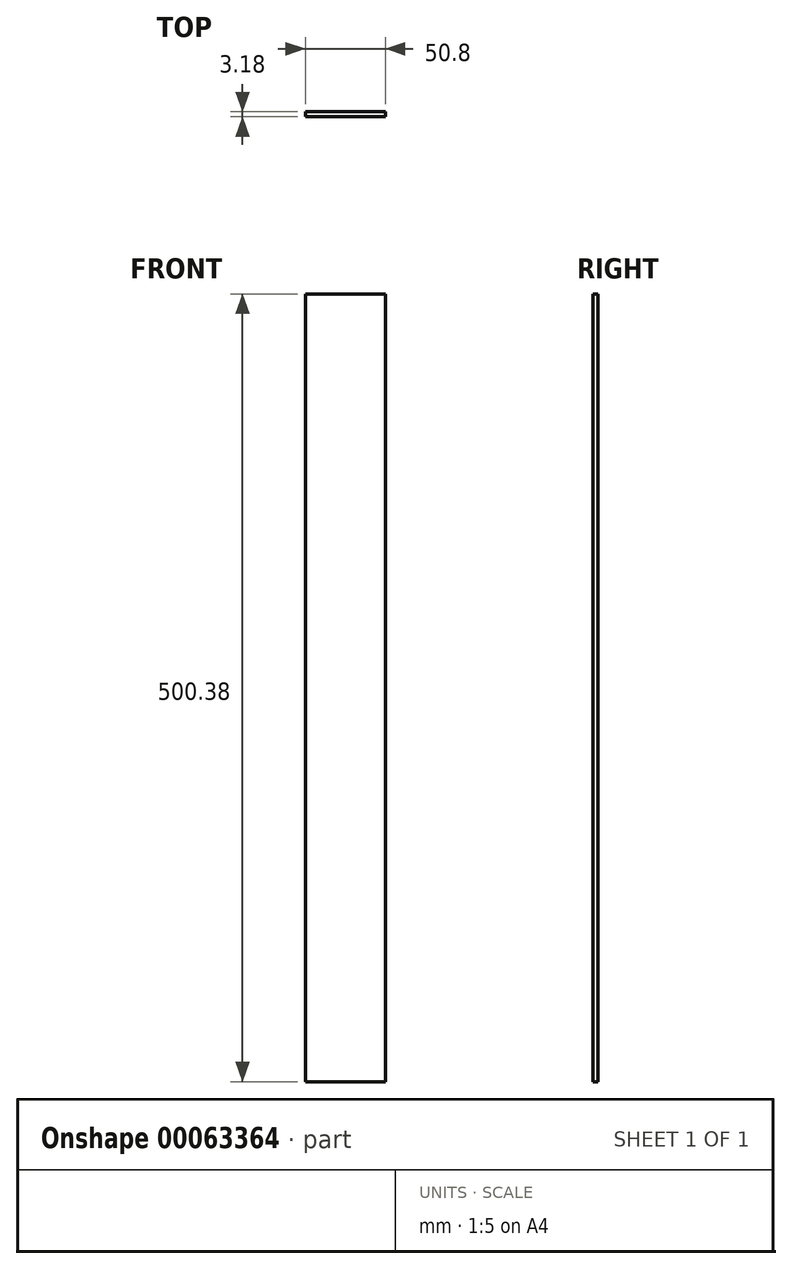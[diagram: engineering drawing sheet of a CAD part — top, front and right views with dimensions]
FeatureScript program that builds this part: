
annotation { "Feature Type Name" : "Feature", "Feature Type Description" : "" }
export const myFeature = defineFeature(function(context is Context, id is Id, definition is map)
    precondition{}
    {
        {
            var Q0;
            Q0=qCreatedBy(makeId("Front.planeOp"),FACE);
            var sketch = newSketch(context, id + "F0", { "sketchPlane" : qUnion([Q0])});
            skLineSegment(sketch, "E0.rect.bottom", {"start": v(25.4, 250.2) * mm, "end": v(-25.4, 250.2) * mm});
            skLineSegment(sketch, "E0.rect.top", {"start": v(25.4, -250.2) * mm, "end": v(-25.4, -250.2) * mm});
            skLineSegment(sketch, "E0.rect.left", {"start": v(25.4, 250.2) * mm, "end": v(25.4, -250.2) * mm});
            skLineSegment(sketch, "E0.rect.right", {"start": v(-25.4, 250.2) * mm, "end": v(-25.4, -250.2) * mm});
            skPoint(sketch, "E0.rect.middle", {"position": v(0, 0) * mm});
            skSolve(sketch);
        }
        {
            var Q0;
            Q0=makeQuery(id+"F0.imprint","IMPRINT",FACE,{"disambiguationData":[TD([[makeQuery(id+"F0.imprint","IMPRINT",EDGE,{"derivedFrom":sQuery(id+"F0.wireOp",EDGE,"E0.rect.bottom")}),1.0]])]});
            extrude(context, id + "F1", {"entities" : qUnion([Q0]), "endBound" : BoundingType.SYMMETRIC, "depth" : 3.17 * mm});
        }
    });
